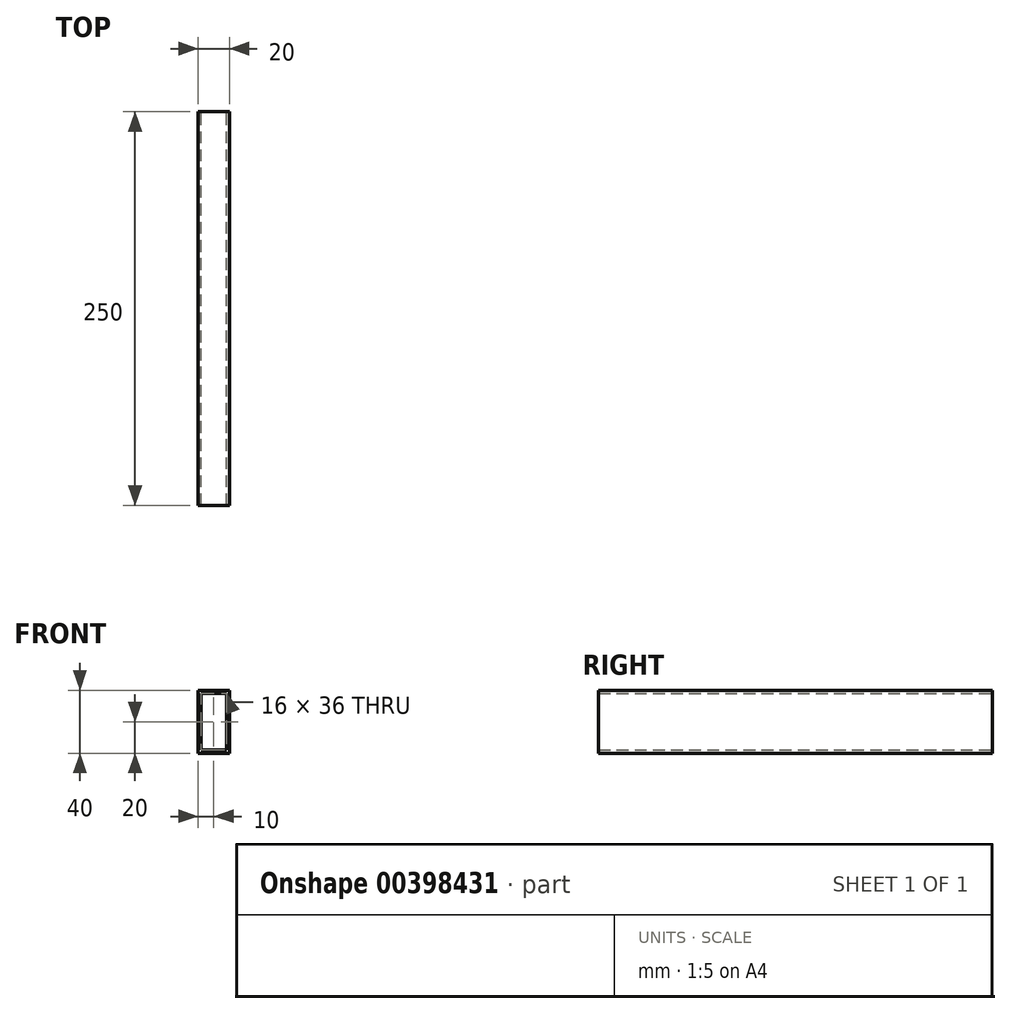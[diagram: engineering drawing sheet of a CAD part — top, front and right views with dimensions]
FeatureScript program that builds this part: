
annotation { "Feature Type Name" : "Feature", "Feature Type Description" : "" }
export const myFeature = defineFeature(function(context is Context, id is Id, definition is map)
    precondition{}
    {
        {
            var Q0;
            Q0=qCreatedBy(makeId("Front.planeOp"),FACE);
            var sketch = newSketch(context, id + "F0", { "sketchPlane" : qUnion([Q0])});
            skLineSegment(sketch, "E0.bottom", {"start": v(0, 0) * mm, "end": v(20, 0) * mm});
            skLineSegment(sketch, "E0.top", {"start": v(0, 40) * mm, "end": v(20, 40) * mm});
            skLineSegment(sketch, "E0.left", {"start": v(0, 0) * mm, "end": v(0, 40) * mm});
            skLineSegment(sketch, "E0.right", {"start": v(20, 0) * mm, "end": v(20, 40) * mm});
            skLineSegment(sketch, "E1.bottom", {"start": v(2, 38) * mm, "end": v(18, 38) * mm});
            skLineSegment(sketch, "E1.top", {"start": v(2, 2) * mm, "end": v(18, 2) * mm});
            skLineSegment(sketch, "E1.left", {"start": v(2, 38) * mm, "end": v(2, 2) * mm});
            skLineSegment(sketch, "E1.right", {"start": v(18, 38) * mm, "end": v(18, 2) * mm});
            skSolve(sketch);
        }
        {
            var Q0;
            Q0=makeQuery(id+"F0.imprint","IMPRINT",FACE,{"disambiguationData":[TD([[makeQuery(id+"F0.imprint","IMPRINT",EDGE,{"derivedFrom":sQuery(id+"F0.wireOp",EDGE,"E0.bottom")}),1.0]])]});
            extrude(context, id + "F1", {"entities" : qUnion([Q0]), "depth" : 250 * mm});
        }
    });
